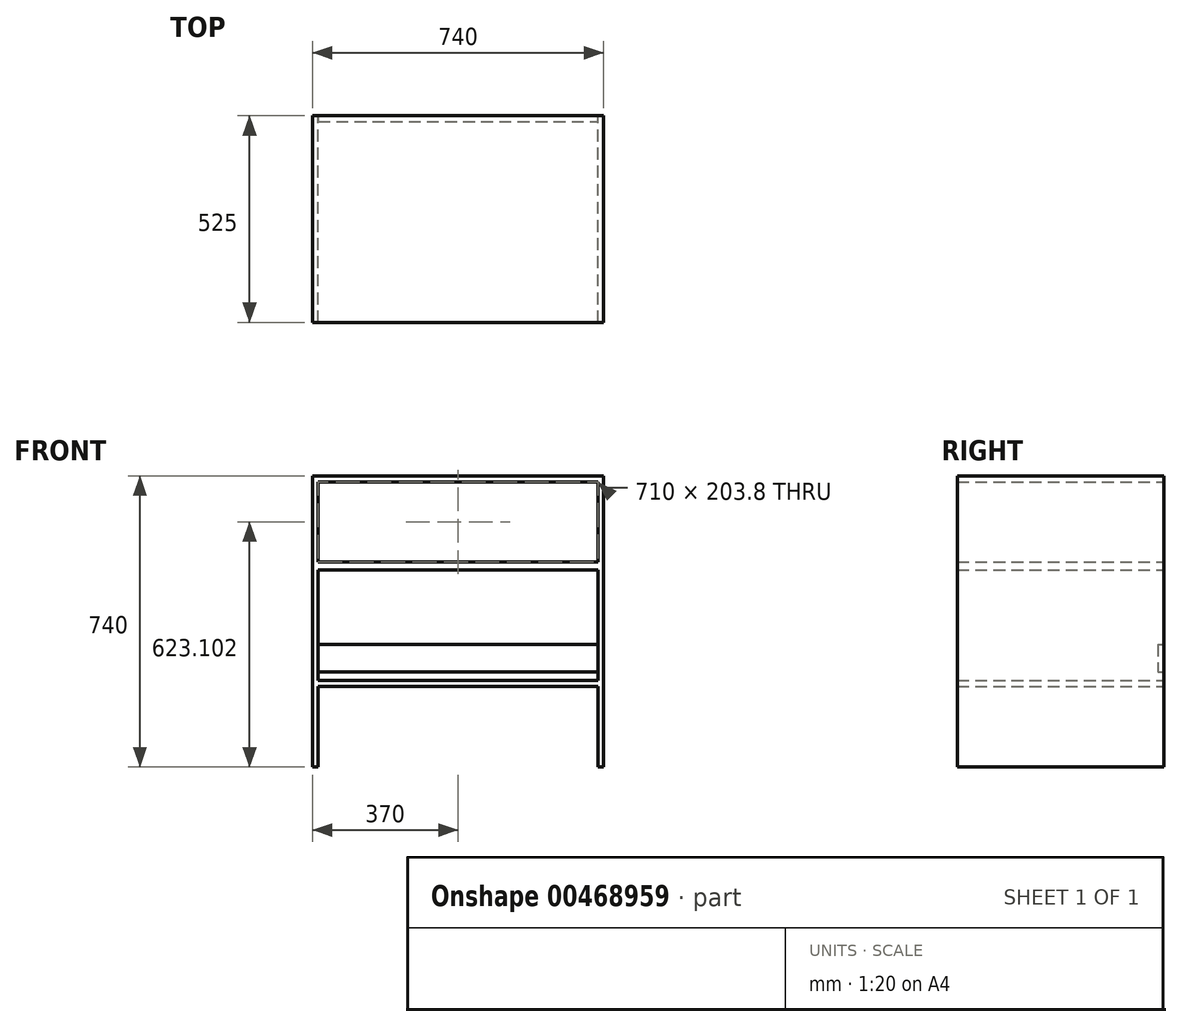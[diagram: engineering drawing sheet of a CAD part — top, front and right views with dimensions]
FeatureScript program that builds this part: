
annotation { "Feature Type Name" : "Feature", "Feature Type Description" : "" }
export const myFeature = defineFeature(function(context is Context, id is Id, definition is map)
    precondition{}
    {
        {
            var Q0;
            Q0=qCreatedBy(makeId("Front.planeOp"),FACE);
            var sketch = newSketch(context, id + "F0", { "sketchPlane" : qUnion([Q0])});
            skLineSegment(sketch, "E0.bottom", {"start": v(370, 370) * mm, "end": v(-370, 370) * mm});
            skLineSegment(sketch, "E0.top", {"start": v(370, -370) * mm, "end": v(355, -370) * mm});
            skLineSegment(sketch, "E0.left", {"start": v(370, 370) * mm, "end": v(370, -370) * mm});
            skLineSegment(sketch, "E0.right", {"start": v(-370, 370) * mm, "end": v(-370, -370) * mm});
            skPoint(sketch, "E0.middle", {"position": v(0, 0) * mm});
            skLineSegment(sketch, "E1.top", {"start": v(-355, -165.29) * mm, "end": v(355, -165.29) * mm});
            skLineSegment(sketch, "E1.left", {"start": v(-355, -370) * mm, "end": v(-355, -165.29) * mm});
            skLineSegment(sketch, "E1.right", {"start": v(355, -370) * mm, "end": v(355, -165.29) * mm});
            skLineSegment(sketch, "E2.bottom", {"start": v(-355, -150.29) * mm, "end": v(355, -150.29) * mm});
            skLineSegment(sketch, "E2.top", {"start": v(-355, 131.2) * mm, "end": v(355, 131.2) * mm});
            skLineSegment(sketch, "E2.left", {"start": v(-355, -150.29) * mm, "end": v(-355, 131.2) * mm});
            skLineSegment(sketch, "E2.right", {"start": v(355, -150.29) * mm, "end": v(355, 131.2) * mm});
            skLineSegment(sketch, "E3.bottom", {"start": v(-355, 355) * mm, "end": v(355, 355) * mm});
            skLineSegment(sketch, "E3.top", {"start": v(-355, 151.2) * mm, "end": v(355, 151.2) * mm});
            skLineSegment(sketch, "E3.left", {"start": v(-355, 355) * mm, "end": v(-355, 151.2) * mm});
            skLineSegment(sketch, "E3.right", {"start": v(355, 355) * mm, "end": v(355, 151.2) * mm});
            skLineSegment(sketch, "E4.trimOffspring", {"start": v(-355, -370) * mm, "end": v(-370, -370) * mm});
            skSolve(sketch);
        }
        {
            var Q0;
            Q0 = qSketchRegion(id + "F0", true);
            extrude(context, id + "F1", {"entities" : qUnion([Q0]), "depth" : 525 * mm});
        }
        {
            var Q0;
            Q0=makeQuery(id+"F1.opExtrude","SWEPT_FACE",FACE,{"disambiguationData":[OSD([sQuery(id+"F0.wireOp",EDGE,"E0.left")])]});
            var sketch = newSketch(context, id + "F2", { "sketchPlane" : qUnion([Q0])});
            skLineSegment(sketch, "E5.bottom", {"start": v(0, -128.43) * mm, "end": v(-15, -128.43) * mm});
            skLineSegment(sketch, "E5.top", {"start": v(0, -58.43) * mm, "end": v(-15, -58.43) * mm});
            skLineSegment(sketch, "E5.left", {"start": v(0, -128.43) * mm, "end": v(0, -58.43) * mm});
            skLineSegment(sketch, "E5.right", {"start": v(-15, -128.43) * mm, "end": v(-15, -58.43) * mm});
            skSolve(sketch);
        }
        {
            var Q0;
            Q0 = qSketchRegion(id + "F2", true);
            var Q1;
            Q1=makeQuery(id+"F1.opExtrude","SWEPT_FACE",FACE,{"disambiguationData":[OSD([sQuery(id+"F0.wireOp",EDGE,"E2.left")])]});
            extrude(context, id + "F3", {"entities" : qUnion([Q0]), "operationType" : NewBodyOperationType.ADD, "endBound" : BoundingType.UP_TO_SURFACE, "oppositeDirection" : true, "endBoundEntityFace" : qUnion([Q1]), "depth" : 25 * mm});
        }
    });
